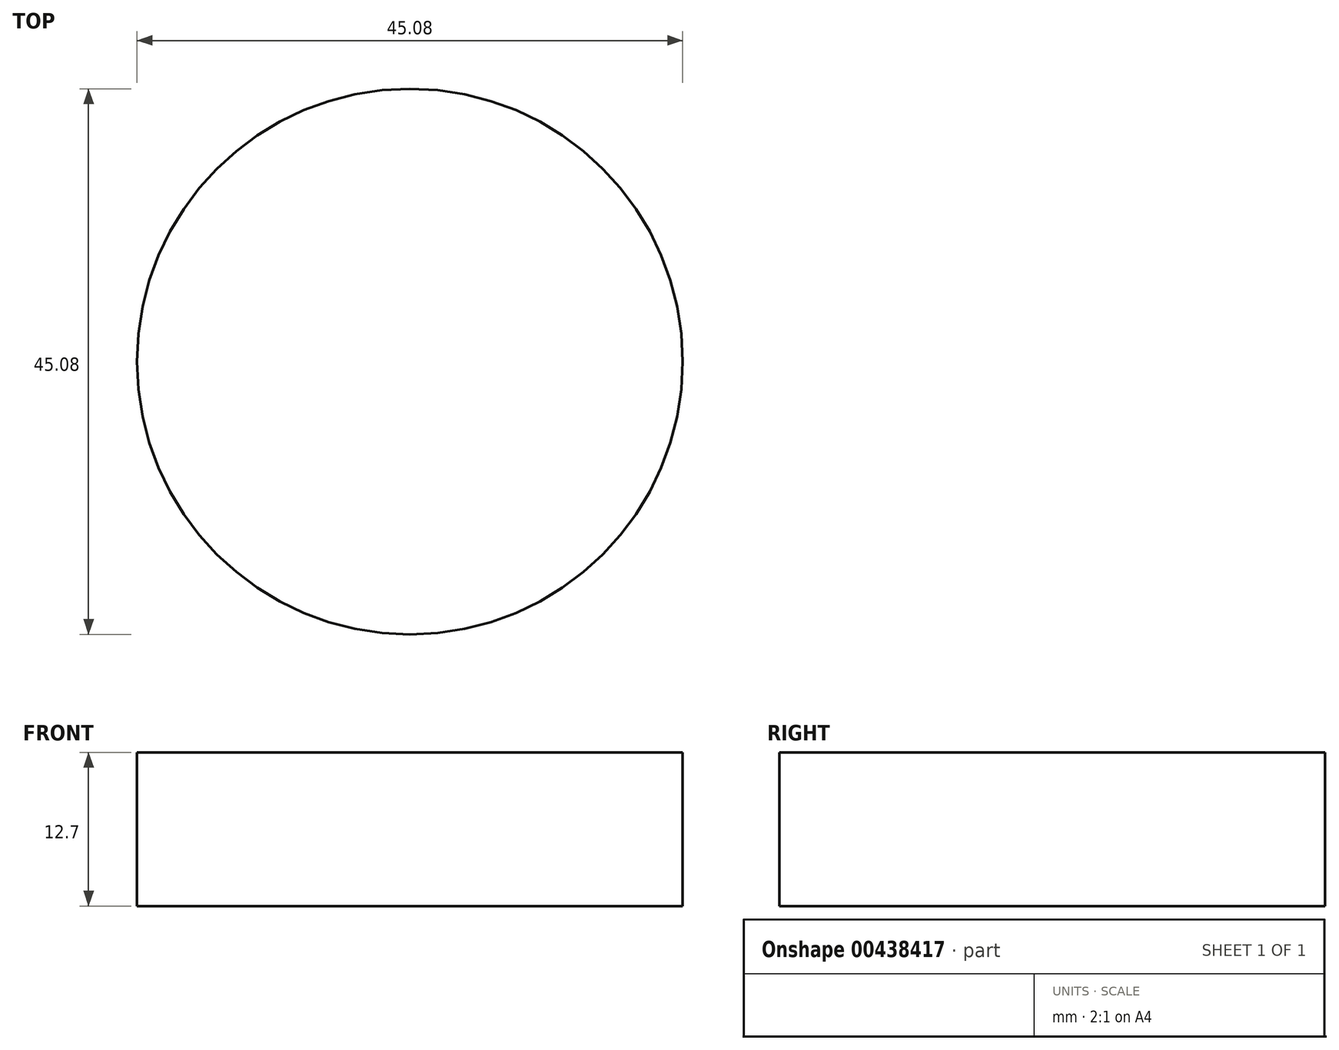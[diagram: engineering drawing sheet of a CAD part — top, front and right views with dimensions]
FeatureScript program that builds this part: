
annotation { "Feature Type Name" : "Feature", "Feature Type Description" : "" }
export const myFeature = defineFeature(function(context is Context, id is Id, definition is map)
    precondition{}
    {
        {
            var Q0;
            Q0=qCreatedBy(makeId("Top.planeOp"),FACE);
            var sketch = newSketch(context, id + "F0", { "sketchPlane" : qUnion([Q0])});
            skCircle(sketch, "E0", {"center": v(0, 0) * mm, "radius": 22.54 * mm});
            skSolve(sketch);
        }
        {
            var Q0;
            Q0=sQuery(id+"F0.wireOp",EDGE,"E0");
            extrude(context, id + "F1", {"bodyType" : ToolBodyType.SURFACE, "surfaceEntities" : qUnion([Q0]), "depth" : 12.95 * mm});
        }
        {
            var Q0;
            Q0 = qSketchRegion(id + "F0", true);
            extrude(context, id + "F2", {"entities" : qUnion([Q0]), "depth" : 12.7 * mm});
        }
        {
            var Q0;
            Q0=qCreatedBy(makeId("Top.planeOp"),FACE);
            var sketch = newSketch(context, id + "F3", { "sketchPlane" : qUnion([Q0])});
            skCircle(sketch, "E1", {"center": v(0, 0) * mm, "radius": 22.69 * mm});
            skSolve(sketch);
        }
        {
            var Q0;
            Q0 = qSketchRegion(id + "F3", true);
            extrude(context, id + "F4", {"entities" : qUnion([Q0]), "operationType" : NewBodyOperationType.REMOVE, "oppositeDirection" : true, "depth" : 2.54 * mm});
        }
    });
